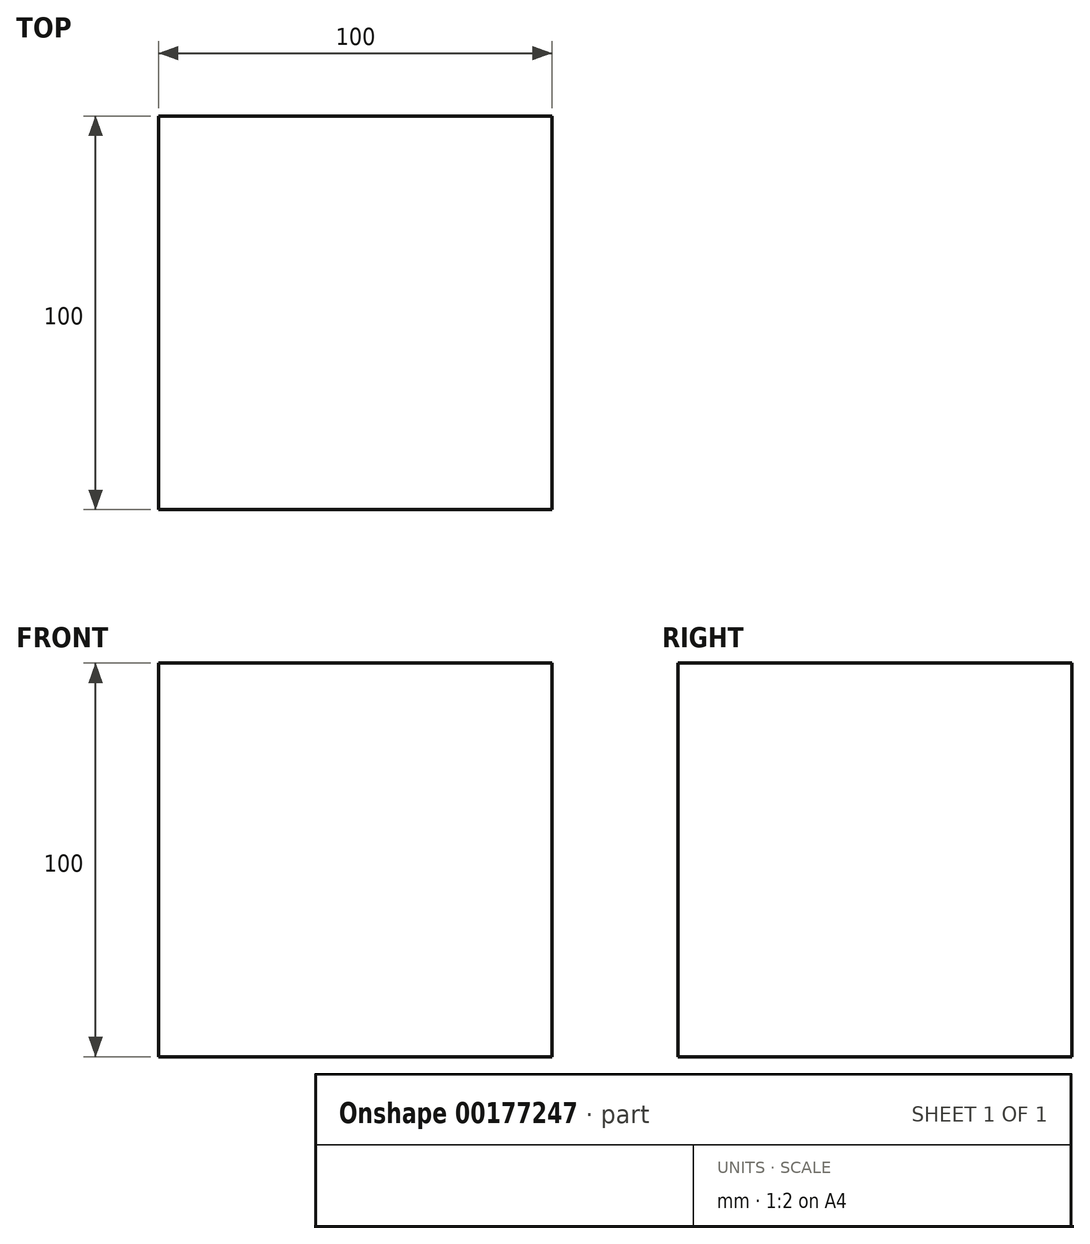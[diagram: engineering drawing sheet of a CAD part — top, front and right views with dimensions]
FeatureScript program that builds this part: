
annotation { "Feature Type Name" : "Feature", "Feature Type Description" : "" }
export const myFeature = defineFeature(function(context is Context, id is Id, definition is map)
    precondition{}
    {
        {
            var Q0;
            Q0=qCreatedBy(makeId("Front.planeOp"),FACE);
            var sketch = newSketch(context, id + "F0", { "sketchPlane" : qUnion([Q0])});
            skLineSegment(sketch, "E0.bottom", {"start": v(-36.4, 74.6) * mm, "end": v(63.6, 74.6) * mm});
            skLineSegment(sketch, "E0.top", {"start": v(-36.4, -25.4) * mm, "end": v(63.6, -25.4) * mm});
            skLineSegment(sketch, "E0.left", {"start": v(-36.4, 74.6) * mm, "end": v(-36.4, -25.4) * mm});
            skLineSegment(sketch, "E0.right", {"start": v(63.6, 74.6) * mm, "end": v(63.6, -25.4) * mm});
            skSolve(sketch);
        }
        {
            var Q0;
            Q0=makeQuery(id+"F0.imprint","IMPRINT",FACE,{"disambiguationData":[TD([[makeQuery(id+"F0.imprint","IMPRINT",EDGE,{"derivedFrom":sQuery(id+"F0.wireOp",EDGE,"E0.bottom")}),-1.0]])]});
            extrude(context, id + "F1", {"entities" : qUnion([Q0]), "depth" : 100 * mm});
        }
    });
